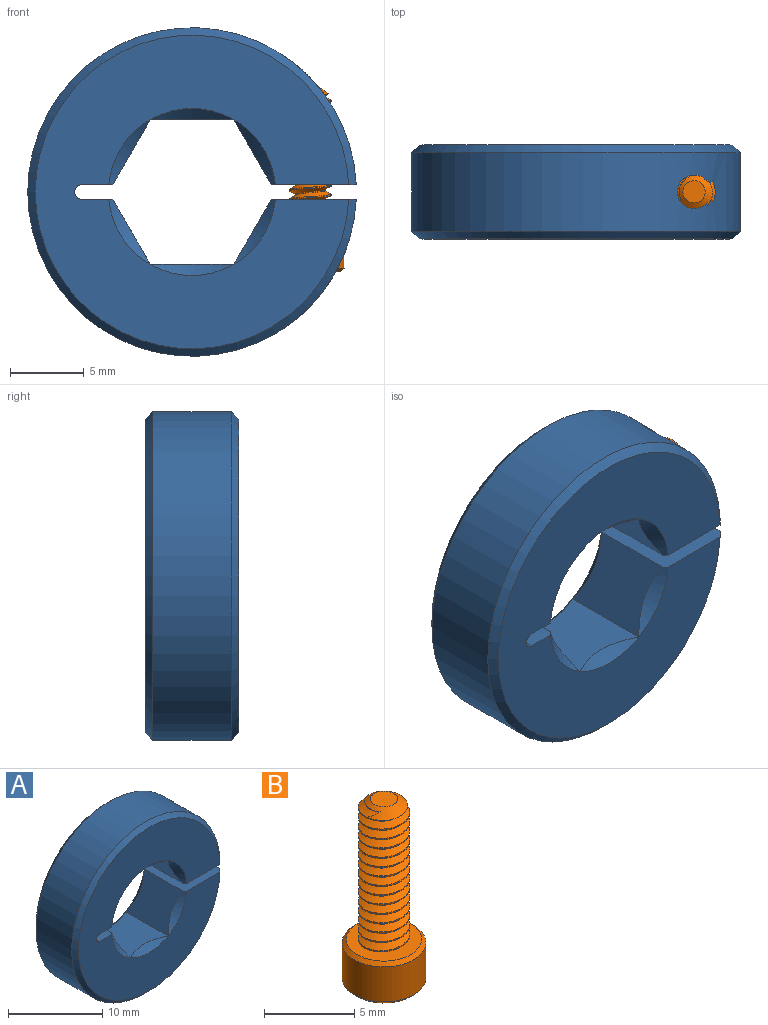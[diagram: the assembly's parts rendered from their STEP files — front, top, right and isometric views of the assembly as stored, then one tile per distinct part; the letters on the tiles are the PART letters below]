
ASSEMBLY  parts=2 mates=1
PART A: 24 faces, bbox 22.2x6.4x22.2 mm
  f0: cone r=10.6mm half-angle=45deg, axis (0,1,0), area 48.3mm2, adj f4,f5,f7,f8
  f1: cylinder r=2.38mm len=7.07mm, axis (0,0,1), area 71.3mm2, adj f4,f9
  f2: cylinder r=1.63mm len=3.26mm, axis (0,0,1), area 20.8mm2, adj f8,f9
  f3: cylinder r=1.13mm len=7.23mm, axis (0,0,-1), area 48.4mm2, adj f4,f7
  f4: cylinder r=11.11mm len=22.23mm, axis (0,1,0), area 334mm2, adj f0,f1,f3,f7,f8,f23
  f5: plane 21.21x21.2mm, normal (0,-1,0), area 245.8mm2, adj f0,f7,f8,f10,f11,f12,f14,f15
  f6: plane 21.21x21.2mm, normal (0,1,0), area 245.8mm2, adj f7,f8,f10,f11,f12,f13,f16,f23
  f7: plane 6.35x5.74mm, normal (0,0,-1), area 32.1mm2, adj f0,f3,f4,f5,f6,f13,f14,f22
  f8: plane 6.35x5.74mm, normal (0,0,1), area 27.8mm2, adj f0,f2,f4,f5,f6,f15,f16,f17
  f9: plane 4.76x4.76mm, normal (0,0,-1), area 9.4mm2, adj f1,f2
  f10: plane 6.35x2.08mm, normal (0,0,1), area 13.1mm2, adj f5,f6,f12,f15,f16,f19
  f11: plane 6.35x2.08mm, normal (0,0,-1), area 13.1mm2, adj f5,f6,f12,f13,f14,f21
  f12: cylinder r=0.5mm len=6.35mm, axis (0,-1,0), area 10mm2, adj f5,f6,f10,f11
  f13: cone r=5.65mm half-angle=45deg, axis (0,1,0), area 12.2mm2, adj f6,f7,f11,f20,f21,f22
  f14: cone r=4.89mm half-angle=45deg, axis (0,-1,0), area 12.2mm2, adj f5,f7,f11,f20,f21,f22
  f15: cone r=4.89mm half-angle=45deg, axis (0,-1,0), area 12.2mm2, adj f5,f8,f10,f17,f18,f19
  f16: cone r=5.65mm half-angle=45deg, axis (0,1,0), area 12.2mm2, adj f6,f8,f10,f17,f18,f19
  f17: plane 6.34x4.39mm, normal (-0.87,0,0.5), area 26.7mm2, adj f8,f15,f16,f18
  f18: plane 6.34x5.65mm, normal (0,0,1), area 30.1mm2, adj f15,f16,f17,f19
  f19: plane 6.34x4.39mm, normal (0.87,0,0.5), area 26.7mm2, adj f10,f15,f16,f18
  f20: plane 6.34x5.65mm, normal (0,0,-1), area 30.2mm2, adj f13,f14,f21,f22
  f21: plane 6.34x4.39mm, normal (0.87,0,-0.5), area 26.7mm2, adj f11,f13,f14,f20
  f22: plane 6.34x4.39mm, normal (-0.87,0,-0.5), area 26.7mm2, adj f7,f13,f14,f20
  f23: cone r=11.11mm half-angle=45deg, axis (0,-1,0), area 48.3mm2, adj f4,f6,f7,f8
PART B: 24 faces, bbox 5.2x5.2x13 mm
  f0: cone r=2.32mm half-angle=45deg, axis (0,0,-1), area 4.6mm2, adj f1,f8
  f1: plane 4.43x4.43mm, normal (0,0,1), area 9mm2, adj f0,f2,f5,f6,f7
  f2: bspline ~9.82x2.84mm, area 52.8mm2, adj f1,f3,f5,f7
  f3: cone r=0.76mm half-angle=55deg, axis (0,0,-1), area 3.6mm2, adj f2,f4,f5,f6,f7
  f4: plane 1.51x1.51mm, normal (0,0,1), area 1.8mm2, adj f3
  f5: cylinder r=1.01mm len=9.35mm, axis (0,0,-1), area 7.4mm2, adj f1,f2,f3,f6
  f6: bspline ~9.59x2.84mm, area 52.8mm2, adj f1,f3,f5,f7
  f7: cylinder r=1.42mm len=9.06mm, axis (0,0,1), area 10.1mm2, adj f1,f2,f3,f6
  f8: cylinder r=2.32mm len=4.65mm, axis (0,0,1), area 34.8mm2, adj f0,f9
  f9: cone r=2.09mm half-angle=45deg, axis (0,0,1), area 4.6mm2, adj f8,f10
  f10: plane 4.63x4.63mm, normal (0,0,-1), area 7.8mm2, adj f9,f11,f19,f20,f21,f22,f23
  f11: cone r=1.37mm half-angle=45deg, axis (0,0,-1), area 0mm2, adj f10,f12
  f12: plane 2.31x1.71mm, normal (-0.5,-0.87,0), area 2.3mm2, adj f11,f13,f17,f18
  f13: plane 2.75x2.38mm, normal (0,0,-1), area 4.9mm2, adj f12,f14,f15,f16,f17,f18
  f14: plane 1.92x1.51mm, normal (1,0,0), area 2.3mm2, adj f13,f15,f18,f22
  f15: plane 2.31x1.71mm, normal (0.5,0.87,0), area 2.3mm2, adj f13,f14,f16,f21
  f16: plane 2.31x1.71mm, normal (-0.5,0.87,0), area 2.3mm2, adj f13,f15,f17,f20
  f17: plane 2.31x1.9mm, normal (-1,0,0), area 2.3mm2, adj f12,f13,f16,f19
  f18: plane 2.31x1.71mm, normal (0.5,-0.87,0), area 2.3mm2, adj f12,f13,f14,f23
  f19: cone r=1.37mm half-angle=45deg, axis (0,0,-1), area 0mm2, adj f10,f17
  f20: cone r=1.37mm half-angle=45deg, axis (0,0,-1), area 0mm2, adj f10,f16
  f21: cone r=1.37mm half-angle=45deg, axis (0,0,-1), area 0mm2, adj f10,f15
  f22: cone r=1.37mm half-angle=45deg, axis (0,0,-1), area 0.2mm2, adj f10,f14
  f23: cone r=1.37mm half-angle=45deg, axis (0,0,-1), area 0mm2, adj f10,f18
PLACE A t=(-11.73,-3.27,5.27)mm
PLACE B t=(-11.73,-3.27,5.27)mm
MATE fastened B.f0 <-> A.f1  axis (0,0,1) through (-3.75,-3.27,2.73)mm
